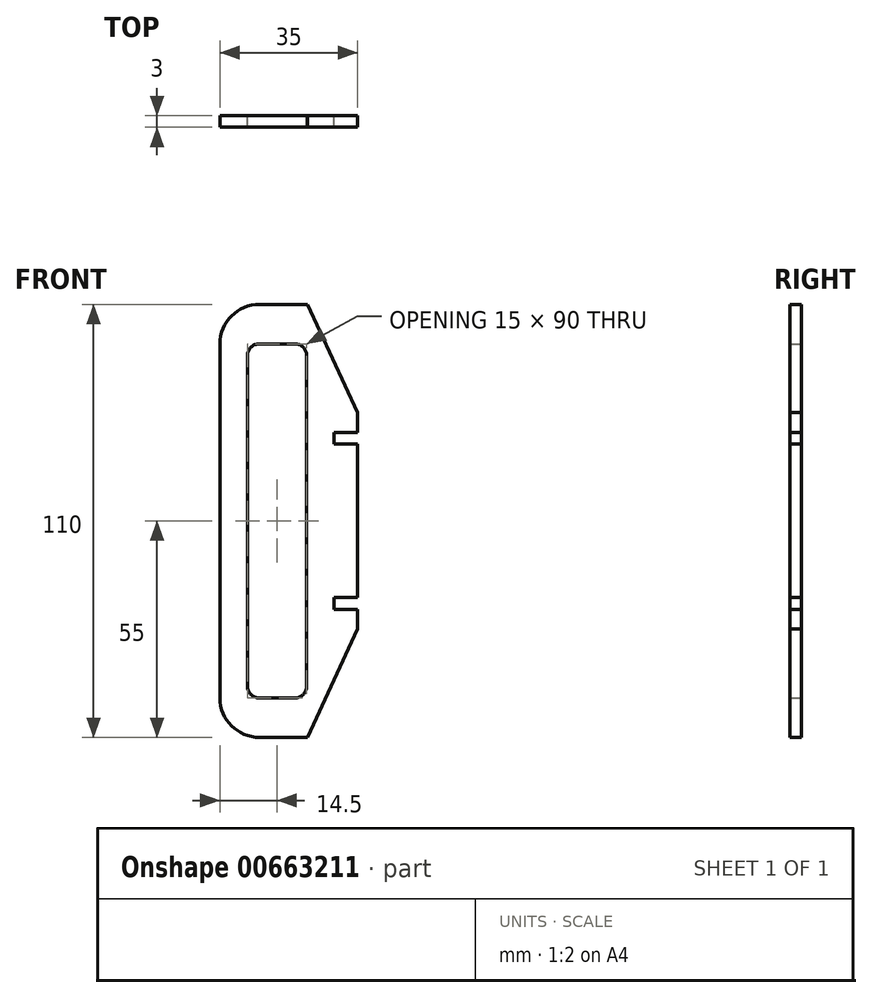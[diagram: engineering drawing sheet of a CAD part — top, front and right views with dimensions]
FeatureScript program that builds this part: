
annotation { "Feature Type Name" : "Feature", "Feature Type Description" : "" }
export const myFeature = defineFeature(function(context is Context, id is Id, definition is map)
    precondition{}
    {
        {
            var Q0;
            Q0=qCreatedBy(makeId("Front.planeOp"),FACE);
            var sketch = newSketch(context, id + "F0", { "sketchPlane" : qUnion([Q0])});
            skLineSegment(sketch, "E0", {"start": v(-35, 0) * mm, "end": v(-35, -45) * mm});
            skLineSegment(sketch, "E1", {"start": v(-25, -55) * mm, "end": v(-12.82, -55) * mm});
            skLineSegment(sketch, "E2", {"start": v(-12.82, -55) * mm, "end": v(0, -27.5) * mm});
            skLineSegment(sketch, "E3", {"start": v(0, -27.5) * mm, "end": v(0, -22.5) * mm});
            skLineSegment(sketch, "E4", {"start": v(0, -22.5) * mm, "end": v(-6, -22.5) * mm});
            skLineSegment(sketch, "E5", {"start": v(-6, -22.5) * mm, "end": v(-6, -19.5) * mm});
            skLineSegment(sketch, "E6", {"start": v(-6, -19.5) * mm, "end": v(0, -19.5) * mm});
            skLineSegment(sketch, "E7", {"start": v(0, -19.5) * mm, "end": v(0, 0) * mm});
            skLineSegment(sketch, "E8", {"start": v(-28, 0) * mm, "end": v(-28, -42) * mm});
            skLineSegment(sketch, "E9", {"start": v(-25, -45) * mm, "end": v(-16, -45) * mm});
            skLineSegment(sketch, "E10", {"start": v(-13, -42) * mm, "end": v(-13, 0) * mm});
            skPoint(sketch, "E11.visualSharp", {"position": v(-28, -45) * mm});
            skArc(sketch, "E11.filletArc", {"start": v(-28, -42) * mm, "mid": v(-27.12, -44.12) * mm, "end": v(-25, -45) * mm});
            skPoint(sketch, "E12.visualSharp", {"position": v(-13, -45) * mm});
            skArc(sketch, "E12.filletArc", {"start": v(-16, -45) * mm, "mid": v(-13.88, -44.12) * mm, "end": v(-13, -42) * mm});
            skPoint(sketch, "E13.visualSharp", {"position": v(-35, -55) * mm});
            skArc(sketch, "E13.filletArc", {"start": v(-35, -45) * mm, "mid": v(-32.07, -52.07) * mm, "end": v(-25, -55) * mm});
            skArc(sketch, "E14.MirrorCS", {"start": v(-28, 42) * mm, "mid": v(-27.12, 44.12) * mm, "end": v(-25, 45) * mm});
            skArc(sketch, "E15.MirrorCS", {"start": v(-16, 45) * mm, "mid": v(-13.88, 44.12) * mm, "end": v(-13, 42) * mm});
            skPoint(sketch, "E16.MirrorP", {"position": v(-13, 45) * mm});
            skLineSegment(sketch, "E17.MirrorCS", {"start": v(-25, 55) * mm, "end": v(-12.82, 55) * mm});
            skLineSegment(sketch, "E18.MirrorCS", {"start": v(-6, 19.5) * mm, "end": v(0, 19.5) * mm});
            skArc(sketch, "E19.MirrorCS", {"start": v(-35, 45) * mm, "mid": v(-32.07, 52.07) * mm, "end": v(-25, 55) * mm});
            skPoint(sketch, "E20.MirrorP", {"position": v(-28, 45) * mm});
            skLineSegment(sketch, "E21.MirrorCS", {"start": v(-6, 22.5) * mm, "end": v(-6, 19.5) * mm});
            skPoint(sketch, "E22.MirrorP", {"position": v(-35, 55) * mm});
            skLineSegment(sketch, "E23.MirrorCS", {"start": v(-25, 45) * mm, "end": v(-16, 45) * mm});
            skLineSegment(sketch, "E24.MirrorCS", {"start": v(0, 22.5) * mm, "end": v(-6, 22.5) * mm});
            skLineSegment(sketch, "E25.MirrorCS", {"start": v(-12.82, 55) * mm, "end": v(0, 27.5) * mm});
            skLineSegment(sketch, "E26.MirrorCS", {"start": v(0, 27.5) * mm, "end": v(0, 22.5) * mm});
            skLineSegment(sketch, "E27.MirrorCS", {"start": v(0, 19.5) * mm, "end": v(0, 0) * mm});
            skLineSegment(sketch, "E28.MirrorCS", {"start": v(-13, 42) * mm, "end": v(-13, 0) * mm});
            skLineSegment(sketch, "E29.MirrorCS", {"start": v(-28, 0) * mm, "end": v(-28, 42) * mm});
            skLineSegment(sketch, "E30.MirrorCS", {"start": v(-35, 0) * mm, "end": v(-35, 45) * mm});
            skSolve(sketch);
        }
        {
            var Q0;
            Q0=qSketchRegion(id+"F0",true);
            extrude(context, id + "F1", {"entities" : qUnion([Q0]), "depth" : 3 * mm, "offsetDistance" : 25 * mm});
        }
    });
